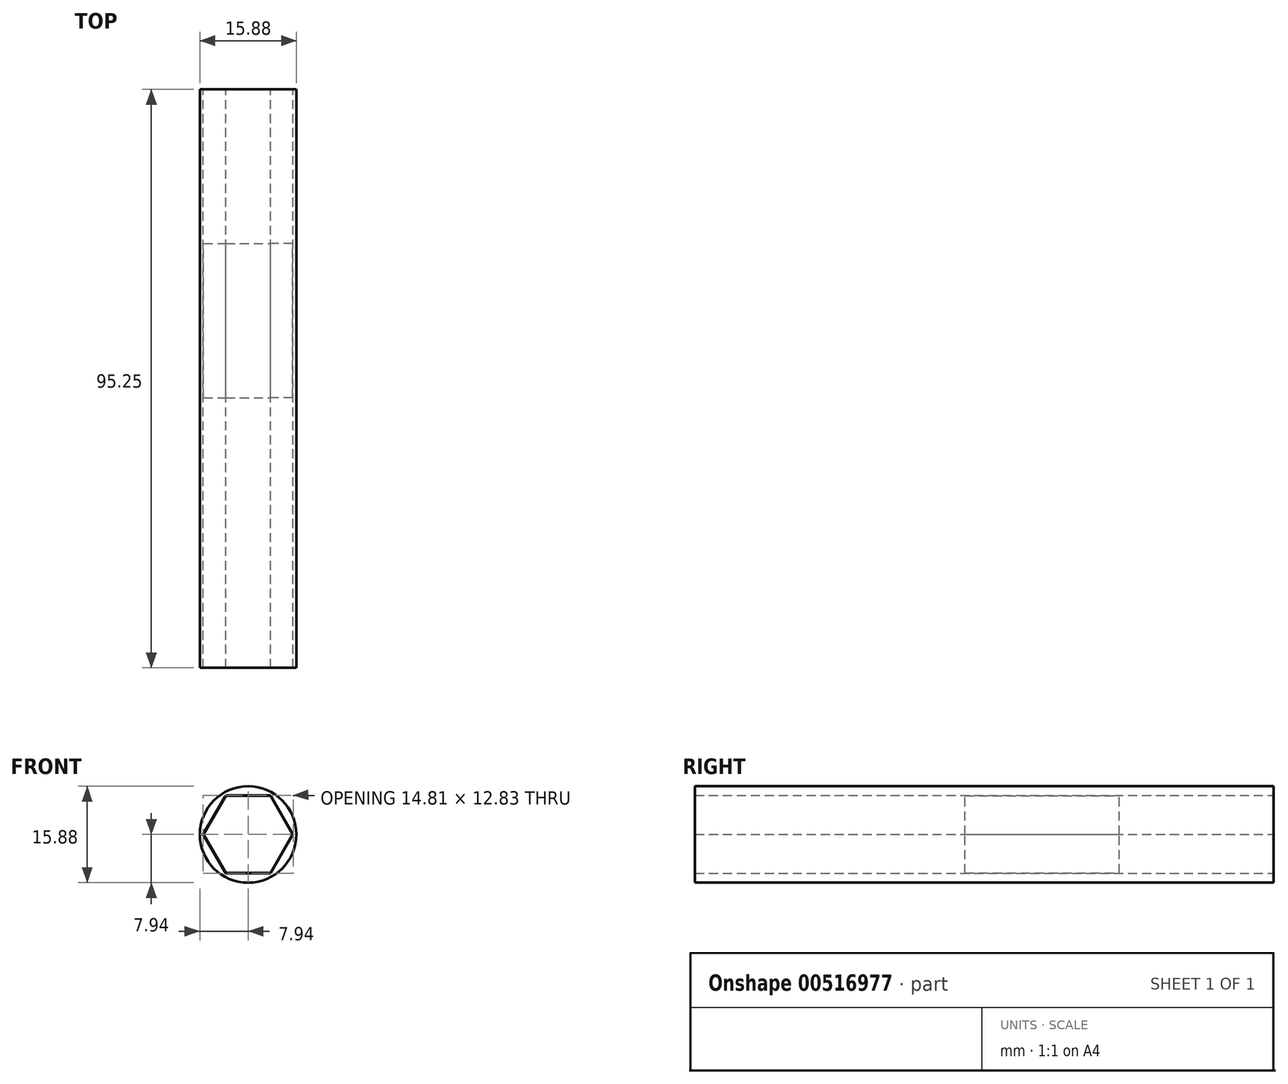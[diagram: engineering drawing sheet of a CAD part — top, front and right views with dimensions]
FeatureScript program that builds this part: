
annotation { "Feature Type Name" : "Feature", "Feature Type Description" : "" }
export const myFeature = defineFeature(function(context is Context, id is Id, definition is map)
    precondition{}
    {
        {
            var Q0;
            Q0=qCreatedBy(makeId("Front.planeOp"),FACE);
            var sketch = newSketch(context, id + "F0", { "sketchPlane" : qUnion([Q0])});
            skCircle(sketch, "E0.cCircle", {"center": v(0, 0) * mm, "radius": 6.35 * mm, "construction": true});
            skLineSegment(sketch, "E0.0", {"start": v(-3.67, 6.35) * mm, "end": v(3.67, 6.35) * mm});
            skLineSegment(sketch, "E0.1", {"start": v(3.67, 6.35) * mm, "end": v(7.33, 0) * mm});
            skLineSegment(sketch, "E0.2", {"start": v(7.33, 0) * mm, "end": v(3.67, -6.35) * mm});
            skLineSegment(sketch, "E0.3", {"start": v(3.67, -6.35) * mm, "end": v(-3.67, -6.35) * mm});
            skLineSegment(sketch, "E0.4", {"start": v(-3.67, -6.35) * mm, "end": v(-7.33, 0) * mm});
            skLineSegment(sketch, "E0.5", {"start": v(-7.33, 0) * mm, "end": v(-3.67, 6.35) * mm});
            skPoint(sketch, "E0.0.midPoint", {"position": v(0, 6.35) * mm});
            skCircle(sketch, "E1.cCircle", {"center": v(0, 0) * mm, "radius": 6.41 * mm, "construction": true});
            skLineSegment(sketch, "E1.0", {"start": v(-3.7, 6.41) * mm, "end": v(3.7, 6.41) * mm});
            skLineSegment(sketch, "E1.1", {"start": v(3.7, 6.41) * mm, "end": v(7.4, 0) * mm});
            skLineSegment(sketch, "E1.2", {"start": v(7.4, 0) * mm, "end": v(3.7, -6.41) * mm});
            skLineSegment(sketch, "E1.3", {"start": v(3.7, -6.41) * mm, "end": v(-3.7, -6.41) * mm});
            skLineSegment(sketch, "E1.4", {"start": v(-3.7, -6.41) * mm, "end": v(-7.4, 0) * mm});
            skLineSegment(sketch, "E1.5", {"start": v(-7.4, 0) * mm, "end": v(-3.7, 6.41) * mm});
            skPoint(sketch, "E1.0.midPoint", {"position": v(0, 6.41) * mm});
            skCircle(sketch, "E2", {"center": v(0, 0) * mm, "radius": 9.53 * mm});
            skCircle(sketch, "E3", {"center": v(0, 0) * mm, "radius": 7.94 * mm});
            skSolve(sketch);
        }
        {
            var Q0;
            Q0=makeQuery(id+"F0.imprint","IMPRINT",FACE,{"disambiguationData":[TD([[makeQuery(id+"F0.imprint","IMPRINT",EDGE,{"derivedFrom":sQuery(id+"F0.wireOp",EDGE,"E0.0")}),-1.0]])]});
            extrude(context, id + "F1", {"entities" : qUnion([Q0]), "depth" : 25.4 * mm, "offsetDistance" : 25.4 * mm});
        }
        {
            var Q0;
            Q0=makeQuery(id+"F0.imprint","IMPRINT",FACE,{"disambiguationData":[TD([[makeQuery(id+"F0.imprint","IMPRINT",EDGE,{"derivedFrom":sQuery(id+"F0.wireOp",EDGE,"E1.0")}),1.0]])]});
            extrude(context, id + "F2", {"entities" : qUnion([Q0]), "depth" : 69.85 * mm, "offsetDistance" : 25.4 * mm});
        }
        {
            var Q0;
            Q0=makeQuery(id+"F0.imprint","IMPRINT",FACE,{"disambiguationData":[TD([[makeQuery(id+"F0.imprint","IMPRINT",EDGE,{"derivedFrom":sQuery(id+"F0.wireOp",EDGE,"E1.0")}),1.0]])]});
            extrude(context, id + "F3", {"entities" : qUnion([Q0]), "operationType" : NewBodyOperationType.ADD, "oppositeDirection" : true, "depth" : 25.4 * mm, "offsetDistance" : 25.4 * mm});
        }
    });
